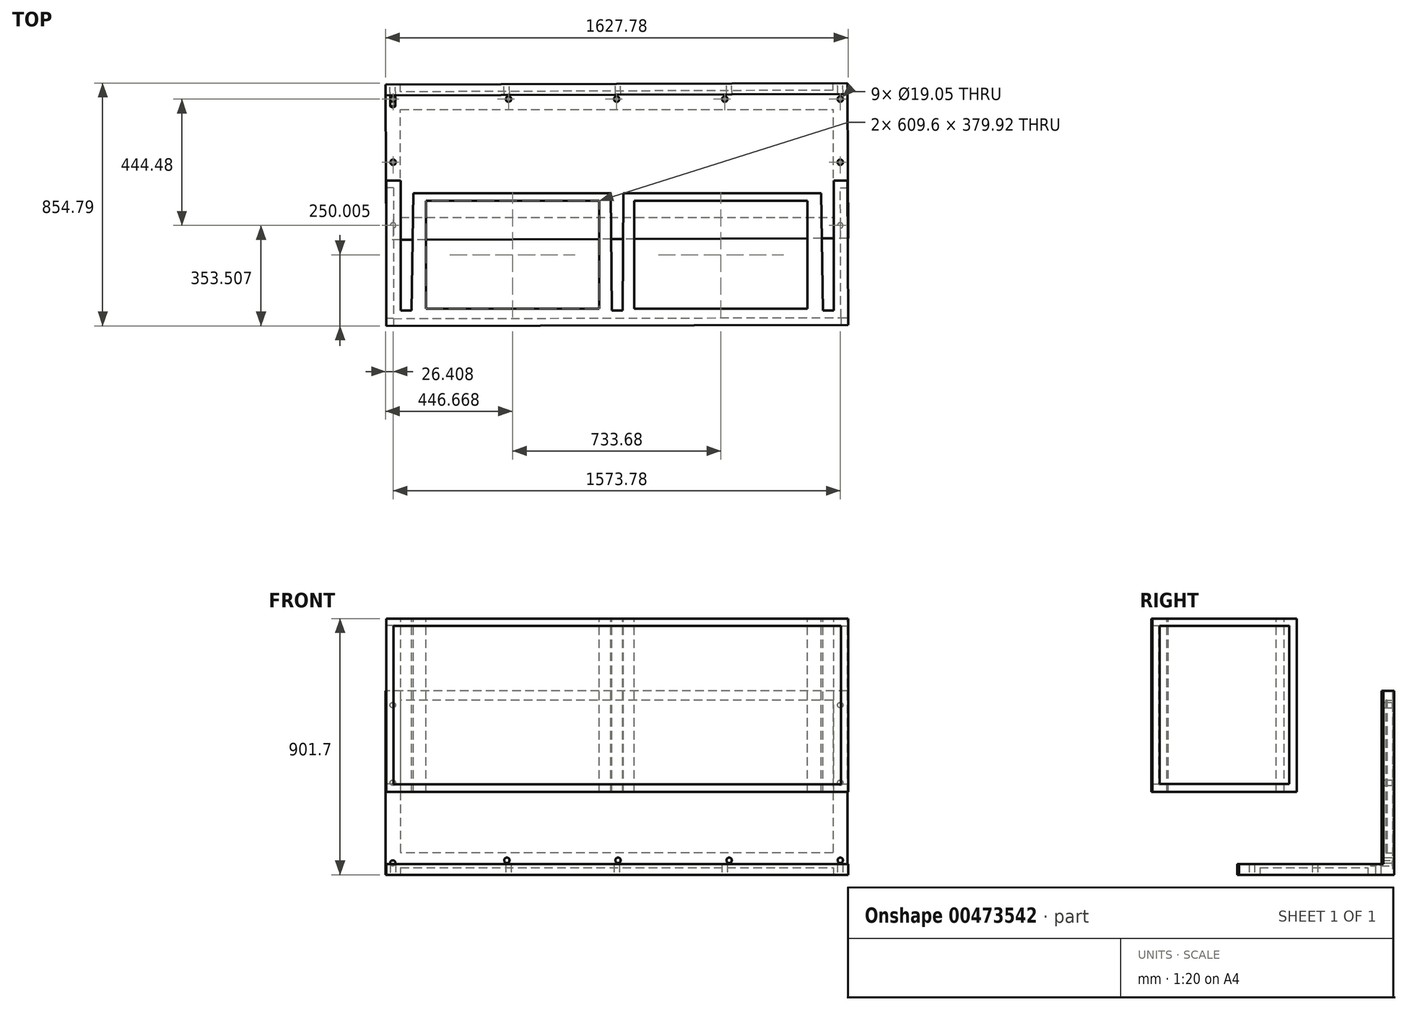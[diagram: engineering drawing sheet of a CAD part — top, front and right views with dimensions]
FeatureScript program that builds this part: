
annotation { "Feature Type Name" : "Feature", "Feature Type Description" : "" }
export const myFeature = defineFeature(function(context is Context, id is Id, definition is map)
    precondition{}
    {
        {
            var Q0;
            Q0=qCreatedBy(makeId("Top.planeOp"),FACE);
            var sketch = newSketch(context, id + "F0", { "sketchPlane" : qUnion([Q0])});
            skLineSegment(sketch, "E0", {"start": v(-1490.15, -82.87) * mm, "end": v(-1490.15, -540.07) * mm});
            skLineSegment(sketch, "E1", {"start": v(-1490.15, -540.07) * mm, "end": v(-1452.05, -540.07) * mm});
            skLineSegment(sketch, "E2", {"start": v(-1490.15, -82.87) * mm, "end": v(33.85, -82.87) * mm});
            skLineSegment(sketch, "E3", {"start": v(33.85, -82.87) * mm, "end": v(33.85, -540.07) * mm});
            skLineSegment(sketch, "E4", {"start": v(33.85, -540.07) * mm, "end": v(-4.25, -540.07) * mm});
            skLineSegment(sketch, "E5", {"start": v(-1445.7, -127.32) * mm, "end": v(-1452.05, -540.07) * mm});
            skLineSegment(sketch, "E6", {"start": v(-10.6, -127.32) * mm, "end": v(-4.25, -540.07) * mm});
            skLineSegment(sketch, "E7", {"start": v(-1445.7, -127.32) * mm, "end": v(-750.38, -127.32) * mm});
            skLineSegment(sketch, "E8", {"start": v(-10.6, -127.32) * mm, "end": v(-705.93, -127.32) * mm});
            skLineSegment(sketch, "E9", {"start": v(-705.93, -127.32) * mm, "end": v(-709.1, -540.07) * mm});
            skLineSegment(sketch, "E10", {"start": v(-750.38, -127.32) * mm, "end": v(-747.2, -540.07) * mm});
            skLineSegment(sketch, "E11", {"start": v(-709.1, -540.07) * mm, "end": v(-747.2, -540.07) * mm});
            skLineSegment(sketch, "E12", {"start": v(33.85, -540.07) * mm, "end": v(33.85, -590.87) * mm});
            skLineSegment(sketch, "E13", {"start": v(82.6, -32.07) * mm, "end": v(84.65, -590.87) * mm});
            skLineSegment(sketch, "E14", {"start": v(-1540.94, -35.7) * mm, "end": v(-1540.94, -594.5) * mm});
            skLineSegment(sketch, "E15", {"start": v(-1540.94, -35.7) * mm, "end": v(82.6, -32.07) * mm});
            skLineSegment(sketch, "E16", {"start": v(-1540.94, -594.5) * mm, "end": v(84.65, -590.87) * mm});
            skSolve(sketch);
        }
        {
            var Q0;
            Q0=makeQuery(id+"F0.imprint","IMPRINT",FACE,{"disambiguationData":[TD([[makeQuery(id+"F0.imprint","IMPRINT",EDGE,{"derivedFrom":sQuery(id+"F0.wireOp",EDGE,"E0")}),-1.0]])]});
            extrude(context, id + "F1", {"entities" : qUnion([Q0]), "depth" : -609.6 * mm});
        }
        {
            var Q0;
            Q0=makeQuery(id+"F1.opExtrude","CAP_FACE",FACE,{"disambiguationData":[OSD([sQuery(id+"F0.wireOp",EDGE,"E0"),sQuery(id+"F0.wireOp",EDGE,"E1"),sQuery(id+"F0.wireOp",EDGE,"E2"),sQuery(id+"F0.wireOp",EDGE,"E3"),sQuery(id+"F0.wireOp",EDGE,"E4"),sQuery(id+"F0.wireOp",EDGE,"E5"),sQuery(id+"F0.wireOp",EDGE,"E6"),sQuery(id+"F0.wireOp",EDGE,"E7"),sQuery(id+"F0.wireOp",EDGE,"E8"),sQuery(id+"F0.wireOp",EDGE,"E9"),sQuery(id+"F0.wireOp",EDGE,"E10"),sQuery(id+"F0.wireOp",EDGE,"E11"),sQuery(id+"F0.wireOp",EDGE,"E13"),sQuery(id+"F0.wireOp",EDGE,"E14"),sQuery(id+"F0.wireOp",EDGE,"E15"),sQuery(id+"F0.wireOp",EDGE,"E16")])],"isStart":true});
            var sketch = newSketch(context, id + "F2", { "sketchPlane" : qUnion([Q0])});
            skLineSegment(sketch, "E17.bottom", {"start": v(-653.62, -154.54) * mm, "end": v(-44.02, -154.54) * mm});
            skLineSegment(sketch, "E17.top", {"start": v(-653.62, -539.96) * mm, "end": v(-44.02, -539.96) * mm});
            skLineSegment(sketch, "E17.left", {"start": v(-653.62, -154.54) * mm, "end": v(-653.62, -539.96) * mm});
            skLineSegment(sketch, "E17.right", {"start": v(-44.02, -154.54) * mm, "end": v(-44.02, -539.96) * mm});
            skLineSegment(sketch, "E18.bottom", {"start": v(-791.66, -154.54) * mm, "end": v(-1401.26, -154.54) * mm});
            skLineSegment(sketch, "E18.top", {"start": v(-791.66, -534.45) * mm, "end": v(-1401.26, -534.45) * mm});
            skLineSegment(sketch, "E18.left", {"start": v(-791.66, -154.54) * mm, "end": v(-791.66, -534.45) * mm});
            skLineSegment(sketch, "E18.right", {"start": v(-1401.26, -154.54) * mm, "end": v(-1401.26, -534.45) * mm});
            skSolve(sketch);
        }
        {
            var Q0;
            Q0=makeQuery(id+"F2.imprint","IMPRINT",FACE,{"disambiguationData":[TD([[makeQuery(id+"F2.imprint","IMPRINT",EDGE,{"derivedFrom":sQuery(id+"F2.wireOp",EDGE,"E18.bottom")}),1.0]])]});
            extrude(context, id + "F3", {"entities" : qUnion([Q0]), "operationType" : NewBodyOperationType.REMOVE, "oppositeDirection" : true, "depth" : 609.6 * mm});
        }
        {
            var Q0;
            Q0=makeQuery(id+"F1.opExtrude","CAP_FACE",FACE,{"disambiguationData":[OSD([sQuery(id+"F0.wireOp",EDGE,"E0"),sQuery(id+"F0.wireOp",EDGE,"E1"),sQuery(id+"F0.wireOp",EDGE,"E2"),sQuery(id+"F0.wireOp",EDGE,"E3"),sQuery(id+"F0.wireOp",EDGE,"E4"),sQuery(id+"F0.wireOp",EDGE,"E5"),sQuery(id+"F0.wireOp",EDGE,"E6"),sQuery(id+"F0.wireOp",EDGE,"E7"),sQuery(id+"F0.wireOp",EDGE,"E8"),sQuery(id+"F0.wireOp",EDGE,"E9"),sQuery(id+"F0.wireOp",EDGE,"E10"),sQuery(id+"F0.wireOp",EDGE,"E11"),sQuery(id+"F0.wireOp",EDGE,"E13"),sQuery(id+"F0.wireOp",EDGE,"E14"),sQuery(id+"F0.wireOp",EDGE,"E15"),sQuery(id+"F0.wireOp",EDGE,"E16")])],"isStart":true});
            var sketch = newSketch(context, id + "F4", { "sketchPlane" : qUnion([Q0])});
            skLineSegment(sketch, "E19.bottom", {"start": v(-667.58, -154.54) * mm, "end": v(-57.98, -154.54) * mm});
            skLineSegment(sketch, "E19.top", {"start": v(-667.58, -534.45) * mm, "end": v(-57.98, -534.45) * mm});
            skLineSegment(sketch, "E19.left", {"start": v(-667.58, -154.54) * mm, "end": v(-667.58, -534.45) * mm});
            skLineSegment(sketch, "E19.right", {"start": v(-57.98, -154.54) * mm, "end": v(-57.98, -534.45) * mm});
            skSolve(sketch);
        }
        {
            var Q0;
            Q0=makeQuery(id+"F4.imprint","IMPRINT",FACE,{"disambiguationData":[TD([[makeQuery(id+"F4.imprint","IMPRINT",EDGE,{"derivedFrom":sQuery(id+"F4.wireOp",EDGE,"E19.bottom")}),-1.0]])]});
            extrude(context, id + "F5", {"entities" : qUnion([Q0]), "operationType" : NewBodyOperationType.REMOVE, "oppositeDirection" : true, "depth" : 609.6 * mm});
        }
        {
            var Q0;
            Q0=makeQuery(id+"F1.opExtrude","CAP_FACE",FACE,{"disambiguationData":[OSD([sQuery(id+"F0.wireOp",EDGE,"E0"),sQuery(id+"F0.wireOp",EDGE,"E1"),sQuery(id+"F0.wireOp",EDGE,"E2"),sQuery(id+"F0.wireOp",EDGE,"E3"),sQuery(id+"F0.wireOp",EDGE,"E4"),sQuery(id+"F0.wireOp",EDGE,"E5"),sQuery(id+"F0.wireOp",EDGE,"E6"),sQuery(id+"F0.wireOp",EDGE,"E7"),sQuery(id+"F0.wireOp",EDGE,"E8"),sQuery(id+"F0.wireOp",EDGE,"E9"),sQuery(id+"F0.wireOp",EDGE,"E10"),sQuery(id+"F0.wireOp",EDGE,"E11"),sQuery(id+"F0.wireOp",EDGE,"E13"),sQuery(id+"F0.wireOp",EDGE,"E14"),sQuery(id+"F0.wireOp",EDGE,"E15"),sQuery(id+"F0.wireOp",EDGE,"E16")])],"isStart":true});
            var sketch = newSketch(context, id + "F6", { "sketchPlane" : qUnion([Q0])});
            skLineSegment(sketch, "E20", {"start": v(-1540.94, -82.87) * mm, "end": v(82.78, -82.87) * mm});
            skLineSegment(sketch, "E21", {"start": v(82.78, -82.87) * mm, "end": v(82.6, -32.07) * mm});
            skLineSegment(sketch, "E22", {"start": v(-1540.94, -35.7) * mm, "end": v(82.6, -32.07) * mm});
            skLineSegment(sketch, "E23", {"start": v(-1540.94, -35.7) * mm, "end": v(-1540.94, -82.87) * mm});
            skSolve(sketch);
        }
        {
            var Q0;
            Q0 = qSketchRegion(id + "F6", true);
            extrude(context, id + "F7", {"entities" : qUnion([Q0]), "operationType" : NewBodyOperationType.REMOVE, "oppositeDirection" : true, "depth" : 609.6 * mm});
        }
        {
            var Q0;
            Q0=makeQuery(id+"F1.opExtrude","SWEPT_FACE",FACE,{"disambiguationData":[OSD([sQuery(id+"F0.wireOp",EDGE,"E13")])]});
            var sketch = newSketch(context, id + "F8", { "sketchPlane" : qUnion([Q0])});
            skLineSegment(sketch, "E24.bottom", {"start": v(-38.1, 0) * mm, "end": v(0, 0) * mm});
            skLineSegment(sketch, "E24.top", {"start": v(-38.1, -609.6) * mm, "end": v(0, -609.6) * mm});
            skLineSegment(sketch, "E24.left", {"start": v(-38.1, 0) * mm, "end": v(-38.1, -609.6) * mm});
            skLineSegment(sketch, "E24.right", {"start": v(0, 0) * mm, "end": v(0, -609.6) * mm});
            skLineSegment(sketch, "E25.bottom", {"start": v(0, -609.6) * mm, "end": v(-546.1, -609.6) * mm});
            skLineSegment(sketch, "E25.top", {"start": v(0, -647.7) * mm, "end": v(-546.1, -647.7) * mm});
            skLineSegment(sketch, "E25.left", {"start": v(0, -609.6) * mm, "end": v(0, -647.7) * mm});
            skLineSegment(sketch, "E25.right", {"start": v(-546.1, -609.6) * mm, "end": v(-546.1, -647.7) * mm});
            skSolve(sketch);
        }
        {
            var Q0;
            Q0=makeQuery(id+"F8.imprint","IMPRINT",FACE,{"disambiguationData":[TD([[makeQuery(id+"F8.imprint","IMPRINT",EDGE,{"derivedFrom":sQuery(id+"F8.wireOp",EDGE,"E24.bottom")}),-1.0]])]});
            var Q1;
            Q1=makeQuery(id+"F8.imprint","IMPRINT",FACE,{"disambiguationData":[TD([[makeQuery(id+"F8.imprint","IMPRINT",EDGE,{"derivedFrom":sQuery(id+"F8.wireOp",EDGE,"E25.top")}),-1.0]])]});
            extrude(context, id + "F9", {"entities" : qUnion([Q0, Q1]), "operationType" : NewBodyOperationType.ADD, "depth" : 1625.6 * mm});
        }
        {
            var Q0;
            Q0=makeQuery(id+"F9.opExtrude","SWEPT_BODY",BODY,{"disambiguationData":[OSD([sQuery(id+"F8.wireOp",EDGE,"E24.bottom"),sQuery(id+"F8.wireOp",EDGE,"E24.left"),sQuery(id+"F8.wireOp",EDGE,"E24.right"),sQuery(id+"F8.wireOp",EDGE,"E25.bottom"),sQuery(id+"F8.wireOp",EDGE,"E25.top"),sQuery(id+"F8.wireOp",EDGE,"E25.left"),sQuery(id+"F8.wireOp",EDGE,"E25.right")])]});
            transform(context, id + "F10", {"entities" : qUnion([Q0]), "transformType" : TransformType.TRANSLATION_3D, "dx" : -1625.6 * mm, "dy" : 254 * mm, "dz" : -254 * mm, "makeCopy" : false});
        }
        {
            var Q0;
            Q0=makeQuery(id+"F1.opExtrude","SWEPT_FACE",FACE,{"disambiguationData":[OSD([sQuery(id+"F0.wireOp",EDGE,"E16")])]});
            var sketch = newSketch(context, id + "F11", { "sketchPlane" : qUnion([Q0])});
            skLineSegment(sketch, "E26", {"start": v(-1465.88, 0) * mm, "end": v(-1465.88, -25.4) * mm});
            skLineSegment(sketch, "E27", {"start": v(-1465.88, -609.6) * mm, "end": v(-1465.88, -584.2) * mm});
            skLineSegment(sketch, "E28", {"start": v(83.33, -561.8) * mm, "end": v(57.93, -561.8) * mm});
            skLineSegment(sketch, "E29", {"start": v(-1542.27, -290.2) * mm, "end": v(-1516.87, -290.2) * mm});
            skLineSegment(sketch, "E30.bottom", {"start": v(-1516.87, -25.4) * mm, "end": v(57.75, -25.4) * mm});
            skLineSegment(sketch, "E30.top", {"start": v(-1516.87, -583.33) * mm, "end": v(57.75, -583.33) * mm});
            skLineSegment(sketch, "E30.left", {"start": v(-1516.87, -25.4) * mm, "end": v(-1516.87, -583.33) * mm});
            skLineSegment(sketch, "E30.right", {"start": v(57.75, -25.4) * mm, "end": v(57.75, -583.33) * mm});
            skSolve(sketch);
        }
        {
            var Q0;
            Q0 = qSketchRegion(id + "F11", true);
            extrude(context, id + "F12", {"entities" : qUnion([Q0]), "operationType" : NewBodyOperationType.REMOVE, "oppositeDirection" : true, "depth" : 25.4 * mm});
        }
        {
            var Q0;
            Q0=makeQuery(id+"F1.opExtrude","SWEPT_FACE",FACE,{"disambiguationData":[OSD([sQuery(id+"F0.wireOp",EDGE,"E13")])]});
            var sketch = newSketch(context, id + "F13", { "sketchPlane" : qUnion([Q0])});
            skLineSegment(sketch, "E31", {"start": v(-591.17, -58.34) * mm, "end": v(-565.77, -58.34) * mm});
            skLineSegment(sketch, "E32", {"start": v(-337.17, 0) * mm, "end": v(-337.17, -25.4) * mm});
            skLineSegment(sketch, "E33", {"start": v(-83.17, -304.8) * mm, "end": v(-108.57, -304.8) * mm});
            skLineSegment(sketch, "E34", {"start": v(-337.17, -609.6) * mm, "end": v(-337.17, -584.2) * mm});
            skLineSegment(sketch, "E35.bottom", {"start": v(-565.77, -25.4) * mm, "end": v(-109.45, -25.4) * mm});
            skLineSegment(sketch, "E35.top", {"start": v(-565.77, -581.67) * mm, "end": v(-109.45, -581.67) * mm});
            skLineSegment(sketch, "E35.left", {"start": v(-565.77, -25.4) * mm, "end": v(-565.77, -581.67) * mm});
            skLineSegment(sketch, "E35.right", {"start": v(-109.45, -25.4) * mm, "end": v(-109.45, -581.67) * mm});
            skSolve(sketch);
        }
        {
            var Q0;
            Q0 = qSketchRegion(id + "F13", true);
            extrude(context, id + "F14", {"entities" : qUnion([Q0]), "operationType" : NewBodyOperationType.REMOVE, "oppositeDirection" : true, "depth" : 25.4 * mm});
        }
        {
            var Q0;
            Q0=makeQuery(id+"F1.opExtrude","SWEPT_FACE",FACE,{"disambiguationData":[OSD([sQuery(id+"F0.wireOp",EDGE,"E14")])]});
            var sketch = newSketch(context, id + "F15", { "sketchPlane" : qUnion([Q0])});
            skLineSegment(sketch, "E36", {"start": v(82.87, -290.2) * mm, "end": v(108.27, -290.2) * mm});
            skLineSegment(sketch, "E37", {"start": v(338.69, 0) * mm, "end": v(338.69, -25.22) * mm});
            skLineSegment(sketch, "E38", {"start": v(594.5, -276.95) * mm, "end": v(569.1, -276.95) * mm});
            skLineSegment(sketch, "E39", {"start": v(338.69, -609.6) * mm, "end": v(338.69, -584.2) * mm});
            skLineSegment(sketch, "E40.bottom", {"start": v(108.27, -25.22) * mm, "end": v(567.89, -25.22) * mm});
            skLineSegment(sketch, "E40.top", {"start": v(108.27, -581.67) * mm, "end": v(567.89, -581.67) * mm});
            skLineSegment(sketch, "E40.left", {"start": v(108.27, -25.22) * mm, "end": v(108.27, -581.67) * mm});
            skLineSegment(sketch, "E40.right", {"start": v(567.89, -25.22) * mm, "end": v(567.89, -581.67) * mm});
            skSolve(sketch);
        }
        {
            var Q0;
            Q0 = qSketchRegion(id + "F15", true);
            extrude(context, id + "F16", {"entities" : qUnion([Q0]), "operationType" : NewBodyOperationType.REMOVE, "oppositeDirection" : true, "depth" : 25.4 * mm});
        }
        {
            var Q0;
            Q0=makeQuery(id+"F9.opExtrude","SWEPT_FACE",FACE,{"disambiguationData":[OSD([sQuery(id+"F8.wireOp",EDGE,"E24.right"),sQuery(id+"F8.wireOp",EDGE,"E25.left")])]});
            var sketch = newSketch(context, id + "F17", { "sketchPlane" : qUnion([Q0])});
            skPoint(sketch, "E41", {"position": v(-58.02, -304.8) * mm});
            skPoint(sketch, "E42", {"position": v(-58.02, -577.85) * mm});
            skPoint(sketch, "E43", {"position": v(-58.02, -850.9) * mm});
            skSolve(sketch);
        }
        {
            var Q0;
            Q0=sQuery(id+"F17.wireOp",VERTEX,"E41");
            var Q1;
            Q1=sQuery(id+"F17.wireOp",VERTEX,"E42");
            var Q2;
            Q2=sQuery(id+"F17.wireOp",VERTEX,"E43");
            var Q3;
            Q3=makeQuery(id+"F9.opExtrude","SWEPT_BODY",BODY,{"disambiguationData":[OSD([sQuery(id+"F8.wireOp",EDGE,"E24.bottom"),sQuery(id+"F8.wireOp",EDGE,"E24.left"),sQuery(id+"F8.wireOp",EDGE,"E24.right"),sQuery(id+"F8.wireOp",EDGE,"E25.bottom"),sQuery(id+"F8.wireOp",EDGE,"E25.top"),sQuery(id+"F8.wireOp",EDGE,"E25.left"),sQuery(id+"F8.wireOp",EDGE,"E25.right")])]});
            hole(context, id + "F18", {"style" : HoleStyle.SIMPLE, "endStyle" : HoleEndStyle.BLIND, "holeDiameter" : 19.05 * mm, "holeDepth" : 76.2 * mm, "isTappedThrough" : true, "tappedDepth" : 12.7 * mm, "tapClearance" : 3, "locations" : qUnion([Q0, Q1, Q2]), "scope" : qUnion([Q3])});
        }
        {
            var Q0;
            Q0=makeQuery(id+"F9.opExtrude","SWEPT_FACE",FACE,{"disambiguationData":[OSD([sQuery(id+"F8.wireOp",EDGE,"E24.right"),sQuery(id+"F8.wireOp",EDGE,"E25.left")])]});
            var sketch = newSketch(context, id + "F19", { "sketchPlane" : qUnion([Q0])});
            skPoint(sketch, "E44", {"position": v(333.14, -850.9) * mm});
            skPoint(sketch, "E45", {"position": v(724.3, -850.9) * mm});
            skPoint(sketch, "E46", {"position": v(1115.46, -850.9) * mm});
            skPoint(sketch, "E47", {"position": v(1516.78, -860.42) * mm});
            skPoint(sketch, "E48", {"position": v(1516.78, -577.85) * mm});
            skPoint(sketch, "E49", {"position": v(1516.78, -304.8) * mm});
            skSolve(sketch);
        }
        {
            var Q0;
            Q0=sQuery(id+"F19.wireOp",VERTEX,"E44");
            var Q1;
            Q1=sQuery(id+"F19.wireOp",VERTEX,"E45");
            var Q2;
            Q2=sQuery(id+"F19.wireOp",VERTEX,"E46");
            var Q3;
            Q3=sQuery(id+"F19.wireOp",VERTEX,"E47");
            var Q4;
            Q4=sQuery(id+"F19.wireOp",VERTEX,"E48");
            var Q5;
            Q5=sQuery(id+"F19.wireOp",VERTEX,"E49");
            var Q6;
            Q6=makeQuery(id+"F9.opExtrude","SWEPT_BODY",BODY,{"disambiguationData":[OSD([sQuery(id+"F8.wireOp",EDGE,"E24.bottom"),sQuery(id+"F8.wireOp",EDGE,"E24.left"),sQuery(id+"F8.wireOp",EDGE,"E24.right"),sQuery(id+"F8.wireOp",EDGE,"E25.bottom"),sQuery(id+"F8.wireOp",EDGE,"E25.top"),sQuery(id+"F8.wireOp",EDGE,"E25.left"),sQuery(id+"F8.wireOp",EDGE,"E25.right")])]});
            hole(context, id + "F20", {"style" : HoleStyle.SIMPLE, "endStyle" : HoleEndStyle.BLIND, "holeDiameter" : 19.05 * mm, "holeDepth" : 76.2 * mm, "isTappedThrough" : true, "tappedDepth" : 12.7 * mm, "tapClearance" : 3, "locations" : qUnion([Q0, Q1, Q2, Q3, Q4, Q5]), "scope" : qUnion([Q6])});
        }
        {
            var Q0;
            Q0=makeQuery(id+"F9.opExtrude","SWEPT_FACE",FACE,{"disambiguationData":[OSD([sQuery(id+"F8.wireOp",EDGE,"E24.right"),sQuery(id+"F8.wireOp",EDGE,"E25.left")])]});
            var sketch = newSketch(context, id + "F21", { "sketchPlane" : qUnion([Q0])});
            skLineSegment(sketch, "E50", {"start": v(-83.42, -374.66) * mm, "end": v(-32.62, -374.66) * mm});
            skLineSegment(sketch, "E51", {"start": v(0, -901.7) * mm, "end": v(0, -825.5) * mm});
            skLineSegment(sketch, "E52", {"start": v(1542.18, -649.58) * mm, "end": v(1491.38, -649.58) * mm});
            skLineSegment(sketch, "E53.bottom", {"start": v(-32.62, -286.88) * mm, "end": v(1490.1, -286.88) * mm});
            skLineSegment(sketch, "E53.top", {"start": v(-32.62, -825.12) * mm, "end": v(1490.1, -825.12) * mm});
            skLineSegment(sketch, "E53.left", {"start": v(-32.62, -286.88) * mm, "end": v(-32.62, -825.12) * mm});
            skLineSegment(sketch, "E53.right", {"start": v(1490.1, -286.88) * mm, "end": v(1490.1, -825.12) * mm});
            skSolve(sketch);
        }
        {
            var Q0;
            {var subQ3=sQuery(id+"F21.wireOp",EDGE,"E53.bottom");Q0=makeQuery(id+"F21.imprint","IMPRINT",FACE,{"disambiguationData":[TD([[makeQuery(id+"F21.imprint","IMPRINT",EDGE,{"derivedFrom":subQ3}),-1.0]])]});}
            extrude(context, id + "F22", {"entities" : qUnion([Q0]), "operationType" : NewBodyOperationType.REMOVE, "oppositeDirection" : true, "depth" : 25.4 * mm});
        }
        {
            var Q0;
            Q0=makeQuery(id+"F9.opExtrude","SWEPT_FACE",FACE,{"disambiguationData":[OSD([sQuery(id+"F8.wireOp",EDGE,"E25.top")])]});
            var sketch = newSketch(context, id + "F23", { "sketchPlane" : qUnion([Q0])});
            skLineSegment(sketch, "E54", {"start": v(-1491.32, 18.75) * mm, "end": v(-1516.72, 18.75) * mm});
            skLineSegment(sketch, "E55", {"start": v(-1491.32, 241) * mm, "end": v(-1516.72, 241) * mm});
            skLineSegment(sketch, "E56", {"start": v(-1491.32, -203.49) * mm, "end": v(-1516.72, -203.49) * mm});
            skLineSegment(sketch, "E57", {"start": v(31.66, 241) * mm, "end": v(57.06, 241) * mm});
            skLineSegment(sketch, "E58", {"start": v(31.66, 18.75) * mm, "end": v(57.06, 18.75) * mm});
            skLineSegment(sketch, "E59", {"start": v(31.66, -203.49) * mm, "end": v(57.06, -203.49) * mm});
            skPoint(sketch, "E60", {"position": v(-1516.72, 241) * mm});
            skPoint(sketch, "E61", {"position": v(-1516.72, 18.75) * mm});
            skPoint(sketch, "E62", {"position": v(-1516.72, -203.49) * mm});
            skLineSegment(sketch, "E63", {"start": v(-1491.32, -203.49) * mm, "end": v(-1491.32, -228.89) * mm});
            skLineSegment(sketch, "E64", {"start": v(-1491.32, -228.89) * mm, "end": v(-1110.32, -228.89) * mm});
            skLineSegment(sketch, "E65", {"start": v(31.66, -203.49) * mm, "end": v(31.66, -228.89) * mm});
            skLineSegment(sketch, "E66", {"start": v(31.66, -228.89) * mm, "end": v(-349.34, -228.89) * mm});
            skLineSegment(sketch, "E67", {"start": v(-1110.32, -228.89) * mm, "end": v(-729.83, -228.89) * mm});
            skPoint(sketch, "E68", {"position": v(-1110.32, -228.89) * mm});
            skPoint(sketch, "E69", {"position": v(-729.83, -228.89) * mm});
            skPoint(sketch, "E70", {"position": v(-349.34, -228.89) * mm});
            skPoint(sketch, "E71", {"position": v(31.66, -228.89) * mm});
            skPoint(sketch, "E72", {"position": v(-1491.32, -228.89) * mm});
            skPoint(sketch, "E73", {"position": v(57.06, -203.49) * mm});
            skPoint(sketch, "E74", {"position": v(57.06, 18.75) * mm});
            skPoint(sketch, "E75", {"position": v(57.06, 241) * mm});
            skPoint(sketch, "E76", {"position": v(-1110.32, -203.49) * mm});
            skPoint(sketch, "E77", {"position": v(-729.83, -203.49) * mm});
            skPoint(sketch, "E78", {"position": v(-349.34, -203.49) * mm});
            skSolve(sketch);
        }
        {
            var Q0;
            Q0=sQuery(id+"F23.wireOp",VERTEX,"E60");
            var Q1;
            Q1=sQuery(id+"F23.wireOp",VERTEX,"E61");
            var Q2;
            Q2=sQuery(id+"F23.wireOp",VERTEX,"E62");
            var Q3;
            Q3=sQuery(id+"F23.wireOp",VERTEX,"E76");
            var Q4;
            Q4=sQuery(id+"F23.wireOp",VERTEX,"E78");
            var Q5;
            Q5=sQuery(id+"F23.wireOp",VERTEX,"E77");
            var Q6;
            Q6=sQuery(id+"F23.wireOp",VERTEX,"E73");
            var Q7;
            Q7=sQuery(id+"F23.wireOp",VERTEX,"E74");
            var Q8;
            Q8=sQuery(id+"F23.wireOp",VERTEX,"E75");
            var Q9;
            Q9=makeQuery(id+"F9.opExtrude","SWEPT_BODY",BODY,{"disambiguationData":[OSD([sQuery(id+"F8.wireOp",EDGE,"E24.bottom"),sQuery(id+"F8.wireOp",EDGE,"E24.left"),sQuery(id+"F8.wireOp",EDGE,"E24.right"),sQuery(id+"F8.wireOp",EDGE,"E25.bottom"),sQuery(id+"F8.wireOp",EDGE,"E25.top"),sQuery(id+"F8.wireOp",EDGE,"E25.left"),sQuery(id+"F8.wireOp",EDGE,"E25.right")])]});
            hole(context, id + "F24", {"style" : HoleStyle.SIMPLE, "endStyle" : HoleEndStyle.BLIND, "holeDiameter" : 19.05 * mm, "holeDepth" : 76.2 * mm, "isTappedThrough" : true, "tappedDepth" : 12.7 * mm, "tapClearance" : 3, "locations" : qUnion([Q0, Q1, Q2, Q3, Q4, Q5, Q6, Q7, Q8]), "scope" : qUnion([Q9])});
        }
        {
            var Q0;
            Q0=makeQuery(id+"F9.opExtrude","SWEPT_FACE",FACE,{"disambiguationData":[OSD([sQuery(id+"F8.wireOp",EDGE,"E25.top")])]});
            var sketch = newSketch(context, id + "F25", { "sketchPlane" : qUnion([Q0])});
            skLineSegment(sketch, "E79", {"start": v(-1541.71, 129.47) * mm, "end": v(-1490.91, 129.28) * mm});
            skLineSegment(sketch, "E80", {"start": v(83.71, 78.8) * mm, "end": v(32.91, 78.98) * mm});
            skLineSegment(sketch, "E81", {"start": v(-728.32, 288.8) * mm, "end": v(-728.32, 212.6) * mm});
            skLineSegment(sketch, "E82.bottom", {"start": v(-1490.91, 212.6) * mm, "end": v(32.91, 212.6) * mm});
            skLineSegment(sketch, "E82.top", {"start": v(-1490.91, -167.3) * mm, "end": v(32.91, -167.3) * mm});
            skLineSegment(sketch, "E82.left", {"start": v(-1490.91, 212.6) * mm, "end": v(-1490.91, -167.3) * mm});
            skLineSegment(sketch, "E82.right", {"start": v(32.91, 212.6) * mm, "end": v(32.91, -167.3) * mm});
            skSolve(sketch);
        }
        {
            var Q0;
            {var subQ4=sQuery(id+"F25.wireOp",EDGE,"E82.top");Q0=makeQuery(id+"F25.imprint","IMPRINT",FACE,{"disambiguationData":[TD([[makeQuery(id+"F25.imprint","IMPRINT",EDGE,{"derivedFrom":subQ4}),1.0]])]});}
            extrude(context, id + "F26", {"entities" : qUnion([Q0]), "operationType" : NewBodyOperationType.REMOVE, "oppositeDirection" : true, "depth" : 25.4 * mm});
        }
    });
